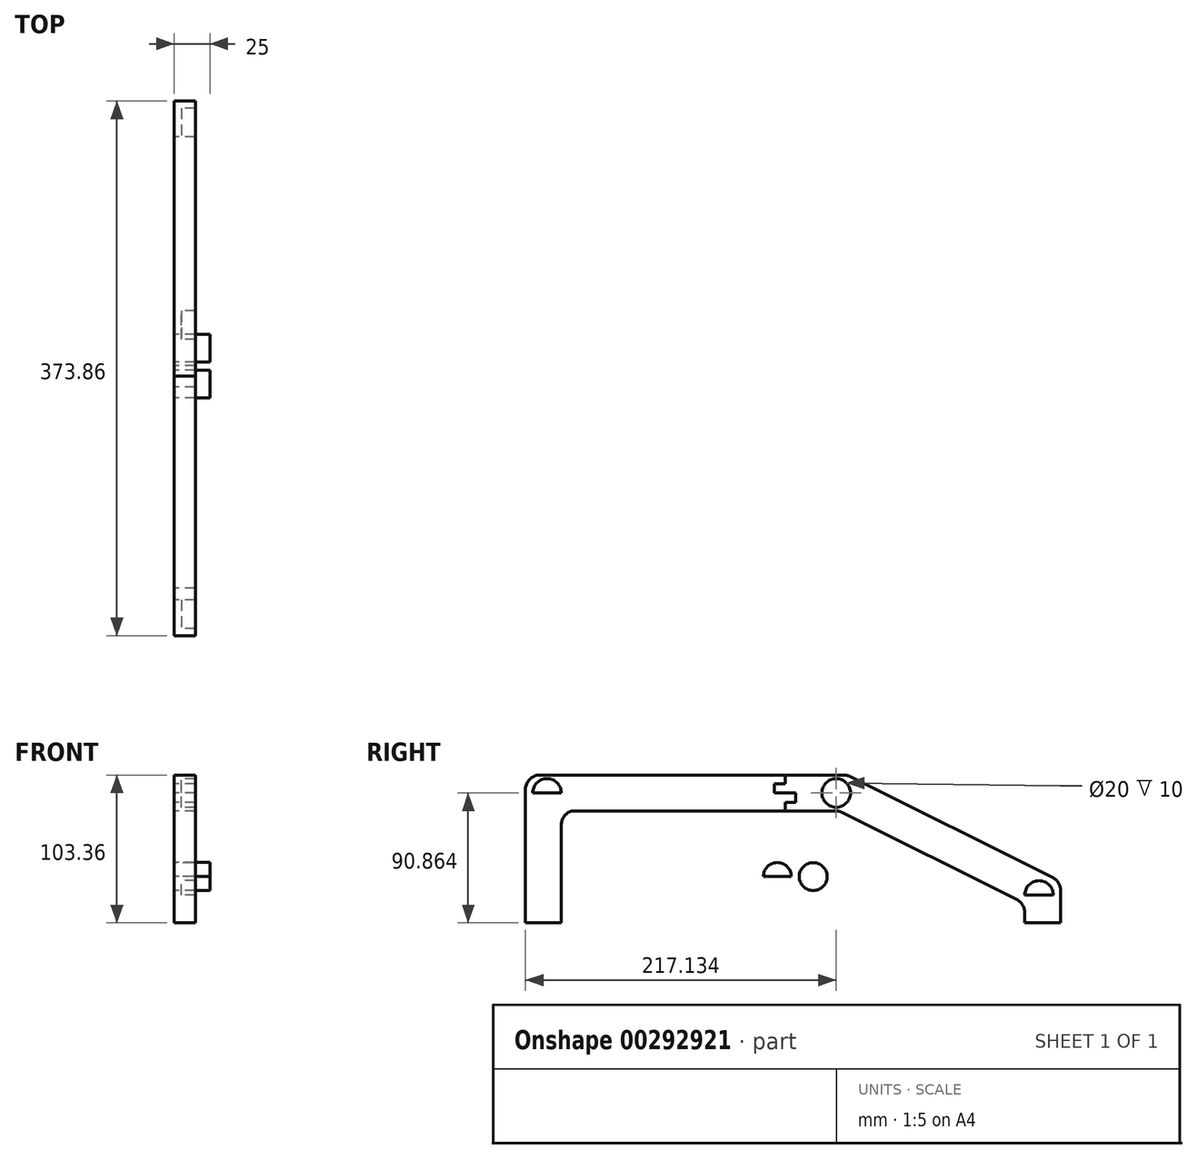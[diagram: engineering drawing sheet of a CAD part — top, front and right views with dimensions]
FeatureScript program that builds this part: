
annotation { "Feature Type Name" : "Feature", "Feature Type Description" : "" }
export const myFeature = defineFeature(function(context is Context, id is Id, definition is map)
    precondition{}
    {
        {
            var Q0;
            Q0=qCreatedBy(makeId("Right.planeOp"),FACE);
            var sketch = newSketch(context, id + "F0", { "sketchPlane" : qUnion([Q0])});
            skCircle(sketch, "E0", {"center": v(-129.4, 35.25) * mm, "radius": 125 * mm});
            skCircle(sketch, "E1", {"center": v(121.3, -39.77) * mm, "radius": 75 * mm});
            skSolve(sketch);
        }
        {
            var Q0;
            Q0=qCreatedBy(makeId("Right.planeOp"),FACE);
            var sketch = newSketch(context, id + "F1", { "sketchPlane" : qUnion([Q0])});
            skCircle(sketch, "E2", {"center": v(-230.46, -54.25) * mm, "radius": 10 * mm});
            skLineSegment(sketch, "E3", {"start": v(-230.46, -54.25) * mm, "end": v(-220.46, -54.25) * mm});
            skLineSegment(sketch, "E4", {"start": v(-220.46, -54.25) * mm, "end": v(-240.46, -54.25) * mm});
            skCircle(sketch, "E5", {"center": v(-28.33, -54.25) * mm, "radius": 10 * mm});
            skCircle(sketch, "E6", {"center": v(56.26, -62.66) * mm, "radius": 75 * mm});
            skCircle(sketch, "E7", {"center": v(113.4, -125.59) * mm, "radius": 10 * mm});
            skLineSegment(sketch, "E8", {"start": v(-28.33, -54.25) * mm, "end": v(-18.33, -54.25) * mm});
            skLineSegment(sketch, "E9", {"start": v(-18.33, -54.25) * mm, "end": v(-38.33, -54.25) * mm});
            skLineSegment(sketch, "E10", {"start": v(113.4, -125.59) * mm, "end": v(123.4, -125.59) * mm});
            skLineSegment(sketch, "E11", {"start": v(123.4, -125.59) * mm, "end": v(103.4, -125.59) * mm});
            skSolve(sketch);
        }
        {
            var Q0;
            Q0=qCreatedBy(makeId("Right.planeOp"),FACE);
            var sketch = newSketch(context, id + "F2", { "sketchPlane" : qUnion([Q0])});
            skLineSegment(sketch, "E12", {"start": v(128.4, -145.11) * mm, "end": v(128.4, -122.28) * mm});
            skLineSegment(sketch, "E13", {"start": v(122.86, -113.33) * mm, "end": v(-18.46, -42.8) * mm});
            skLineSegment(sketch, "E14", {"start": v(-245.46, -51.75) * mm, "end": v(-245.46, -145.11) * mm});
            skLineSegment(sketch, "E15", {"start": v(-245.46, -145.11) * mm, "end": v(-220.46, -145.11) * mm});
            skLineSegment(sketch, "E16", {"start": v(-220.46, -145.11) * mm, "end": v(-220.46, -76.57) * mm});
            skLineSegment(sketch, "E17", {"start": v(103.4, -137.74) * mm, "end": v(103.4, -145.11) * mm});
            skLineSegment(sketch, "E18", {"start": v(103.4, -145.11) * mm, "end": v(128.4, -145.11) * mm});
            skPoint(sketch, "E19.visualSharp", {"position": v(128.4, -116.1) * mm});
            skArc(sketch, "E19.filletArc", {"start": v(128.4, -122.28) * mm, "mid": v(126.9, -117.02) * mm, "end": v(122.86, -113.33) * mm});
            skPoint(sketch, "E20.visualSharp", {"position": v(-15.8, -44.13) * mm});
            skArc(sketch, "E20.filletArc", {"start": v(-18.46, -42.8) * mm, "mid": v(-20.63, -42.01) * mm, "end": v(-22.92, -41.75) * mm});
            skPoint(sketch, "E21.visualSharp", {"position": v(-220.46, -68.46) * mm});
            skArc(sketch, "E21.filletArc", {"start": v(-212.34, -66.75) * mm, "mid": v(-218.17, -70.2) * mm, "end": v(-220.46, -76.57) * mm});
            skLineSegment(sketch, "E22", {"start": v(-22.92, -41.75) * mm, "end": v(-235.46, -41.75) * mm});
            skPoint(sketch, "E23.visualSharp", {"position": v(-245.46, -41.75) * mm});
            skArc(sketch, "E23.filletArc", {"start": v(-235.46, -41.75) * mm, "mid": v(-242.53, -44.67) * mm, "end": v(-245.46, -51.75) * mm});
            skLineSegment(sketch, "E24", {"start": v(97.86, -128.8) * mm, "end": v(-24.35, -67.8) * mm});
            skLineSegment(sketch, "E25", {"start": v(-28.82, -66.75) * mm, "end": v(-212.34, -66.75) * mm});
            skPoint(sketch, "E26.visualSharp", {"position": v(-26.46, -66.75) * mm});
            skArc(sketch, "E26.filletArc", {"start": v(-24.35, -67.8) * mm, "mid": v(-26.52, -67.01) * mm, "end": v(-28.82, -66.75) * mm});
            skPoint(sketch, "E27.visualSharp", {"position": v(103.4, -131.56) * mm});
            skArc(sketch, "E27.filletArc", {"start": v(103.4, -137.74) * mm, "mid": v(101.9, -132.48) * mm, "end": v(97.86, -128.8) * mm});
            skLineSegment(sketch, "E28", {"start": v(-64.05, -66.75) * mm, "end": v(-64.05, -60.75) * mm});
            skLineSegment(sketch, "E29", {"start": v(-64.05, -60.75) * mm, "end": v(-56.55, -60.75) * mm});
            skLineSegment(sketch, "E30", {"start": v(-56.55, -60.75) * mm, "end": v(-56.55, -54.19) * mm});
            skLineSegment(sketch, "E31", {"start": v(-56.55, -54.19) * mm, "end": v(-71.55, -54.19) * mm});
            skLineSegment(sketch, "E32", {"start": v(-71.55, -54.19) * mm, "end": v(-71.55, -47.75) * mm});
            skLineSegment(sketch, "E33", {"start": v(-71.55, -47.75) * mm, "end": v(-64.05, -47.75) * mm});
            skLineSegment(sketch, "E34", {"start": v(-64.05, -47.75) * mm, "end": v(-64.05, -41.75) * mm});
            skSolve(sketch);
        }
        {
            var Q0;
            Q0=makeQuery(id+"F2.imprint","IMPRINT",FACE,{"disambiguationData":[TD([[makeQuery(id+"F2.imprint","IMPRINT",EDGE,{"derivedFrom":sQuery(id+"F2.wireOp",EDGE,"E14")}),1.0]])]});
            extrude(context, id + "F3", {"entities" : qUnion([Q0]), "depth" : 15 * mm});
        }
        {
            var Q0;
            {var subQ0=sQuery(id+"F1.wireOp",EDGE,"E4");var subQ4=makeQuery(id+"F1.imprint","IMPRINT",VERTEX,{"derivedFrom":subQ0});Q0=makeQuery(id+"F1.imprint","IMPRINT",FACE,{"disambiguationData":[TD([[makeQuery(id+"F1.imprint","IMPRINT",EDGE,{"disambiguationData":[TD([[subQ4,1.0]])],"derivedFrom":subQ0}),-1.0]])]});}
            extrude(context, id + "F4", {"entities" : qUnion([Q0]), "operationType" : NewBodyOperationType.REMOVE, "depth" : 25 * mm});
        }
        {
            var Q0;
            Q0=makeQuery(id+"F2.imprint","IMPRINT",FACE,{"disambiguationData":[TD([[makeQuery(id+"F2.imprint","IMPRINT",EDGE,{"derivedFrom":sQuery(id+"F2.wireOp",EDGE,"E12")}),1.0]])]});
            extrude(context, id + "F5", {"entities" : qUnion([Q0]), "depth" : 15 * mm});
        }
        {
            var Q0;
            {var subQ0=sQuery(id+"F1.wireOp",EDGE,"E11");var subQ4=makeQuery(id+"F1.imprint","IMPRINT",VERTEX,{"derivedFrom":subQ0});Q0=makeQuery(id+"F1.imprint","IMPRINT",FACE,{"disambiguationData":[TD([[makeQuery(id+"F1.imprint","IMPRINT",EDGE,{"disambiguationData":[TD([[subQ4,1.0]])],"derivedFrom":subQ0}),-1.0]])]});}
            extrude(context, id + "F6", {"entities" : qUnion([Q0]), "operationType" : NewBodyOperationType.REMOVE, "depth" : 25 * mm});
        }
        {
            var Q0;
            {var subQ0=sQuery(id+"F1.wireOp",EDGE,"E9");var subQ4=makeQuery(id+"F1.imprint","IMPRINT",VERTEX,{"derivedFrom":subQ0});Q0=makeQuery(id+"F1.imprint","IMPRINT",FACE,{"disambiguationData":[TD([[makeQuery(id+"F1.imprint","IMPRINT",EDGE,{"disambiguationData":[TD([[subQ4,1.0]])],"derivedFrom":subQ0}),-1.0]])]});}
            var Q1;
            {var subQ0=sQuery(id+"F1.wireOp",EDGE,"E9");var subQ5=makeQuery(id+"F1.imprint","IMPRINT",VERTEX,{"derivedFrom":subQ0});Q1=makeQuery(id+"F1.imprint","IMPRINT",FACE,{"disambiguationData":[TD([[makeQuery(id+"F1.imprint","IMPRINT",EDGE,{"disambiguationData":[TD([[subQ5,1.0]])],"derivedFrom":subQ0}),1.0]])]});}
            extrude(context, id + "F7", {"entities" : qUnion([Q0, Q1]), "operationType" : NewBodyOperationType.REMOVE, "depth" : 25 * mm});
        }
        {
            var Q0;
            Q0=qCreatedBy(makeId("Right.planeOp"),FACE);
            var sketch = newSketch(context, id + "F8", { "sketchPlane" : qUnion([Q0])});
            skCircle(sketch, "E35", {"center": v(-44.43, -112.72) * mm, "radius": 9.75 * mm});
            skCircle(sketch, "E36", {"center": v(-69.47, -112.64) * mm, "radius": 9.75 * mm});
            skLineSegment(sketch, "E37", {"start": v(-69.47, -112.64) * mm, "end": v(-79.22, -112.64) * mm});
            skLineSegment(sketch, "E38", {"start": v(-79.22, -112.64) * mm, "end": v(-59.72, -112.64) * mm});
            skSolve(sketch);
        }
        {
            var Q0;
            Q0=makeQuery(id+"F8.imprint","IMPRINT",FACE,{"disambiguationData":[TD([[makeQuery(id+"F8.imprint","IMPRINT",EDGE,{"derivedFrom":sQuery(id+"F8.wireOp",EDGE,"E35")}),1.0]])]});
            var Q1;
            {var subQ0=sQuery(id+"F8.wireOp",EDGE,"E38");var subQ4=makeQuery(id+"F8.imprint","IMPRINT",VERTEX,{"derivedFrom":subQ0});Q1=makeQuery(id+"F8.imprint","IMPRINT",FACE,{"disambiguationData":[TD([[makeQuery(id+"F8.imprint","IMPRINT",EDGE,{"disambiguationData":[TD([[subQ4,1.0]])],"derivedFrom":subQ0}),1.0]])]});}
            extrude(context, id + "F9", {"entities" : qUnion([Q0, Q1]), "depth" : 25 * mm});
        }
        {
            var Q0;
            {var subQ0=sQuery(id+"F1.wireOp",EDGE,"E4");var subQ4=makeQuery(id+"F1.imprint","IMPRINT",VERTEX,{"derivedFrom":subQ0});Q0=makeQuery(id+"F1.imprint","IMPRINT",FACE,{"disambiguationData":[TD([[makeQuery(id+"F1.imprint","IMPRINT",EDGE,{"disambiguationData":[TD([[subQ4,1.0]])],"derivedFrom":subQ0}),-1.0]])]});}
            extrude(context, id + "F10", {"entities" : qUnion([Q0]), "operationType" : NewBodyOperationType.ADD, "depth" : 5 * mm});
        }
        {
            var Q0;
            {var subQ0=sQuery(id+"F1.wireOp",EDGE,"E9");var subQ5=makeQuery(id+"F1.imprint","IMPRINT",VERTEX,{"derivedFrom":subQ0});Q0=makeQuery(id+"F1.imprint","IMPRINT",FACE,{"disambiguationData":[TD([[makeQuery(id+"F1.imprint","IMPRINT",EDGE,{"disambiguationData":[TD([[subQ5,1.0]])],"derivedFrom":subQ0}),1.0]])]});}
            var Q1;
            {var subQ0=sQuery(id+"F1.wireOp",EDGE,"E9");var subQ4=makeQuery(id+"F1.imprint","IMPRINT",VERTEX,{"derivedFrom":subQ0});Q1=makeQuery(id+"F1.imprint","IMPRINT",FACE,{"disambiguationData":[TD([[makeQuery(id+"F1.imprint","IMPRINT",EDGE,{"disambiguationData":[TD([[subQ4,1.0]])],"derivedFrom":subQ0}),-1.0]])]});}
            extrude(context, id + "F11", {"entities" : qUnion([Q0, Q1]), "operationType" : NewBodyOperationType.ADD, "depth" : 5 * mm});
        }
        {
            var Q0;
            {var subQ0=sQuery(id+"F1.wireOp",EDGE,"E11");var subQ4=makeQuery(id+"F1.imprint","IMPRINT",VERTEX,{"derivedFrom":subQ0});Q0=makeQuery(id+"F1.imprint","IMPRINT",FACE,{"disambiguationData":[TD([[makeQuery(id+"F1.imprint","IMPRINT",EDGE,{"disambiguationData":[TD([[subQ4,1.0]])],"derivedFrom":subQ0}),-1.0]])]});}
            extrude(context, id + "F12", {"entities" : qUnion([Q0]), "operationType" : NewBodyOperationType.ADD, "depth" : 5 * mm});
        }
    });
